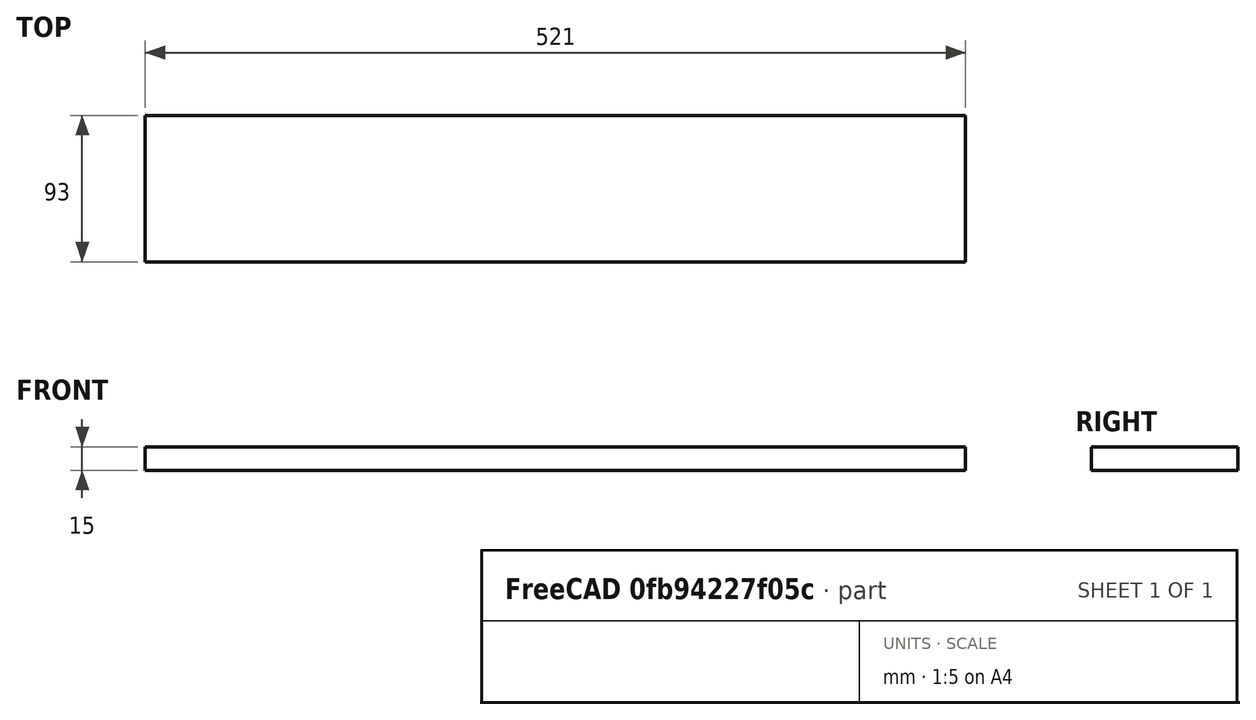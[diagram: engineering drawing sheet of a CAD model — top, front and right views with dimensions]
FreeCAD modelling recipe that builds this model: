
FCSTD DOCUMENT  (FreeCAD 1.0R39109 (Git))
Label: 17_drawer_96mm_front
License: All rights reserved
LicenseURL: http://en.wikipedia.org/wiki/All_rights_reserved
objects: Spreadsheet::Sheet×1, Sketcher::SketchObject×1, PartDesign::Pad×1, PartDesign::Body×1
note: 6 computed .brp shape members not serialized (recipe doc carries the construction recipe); baked Part::Feature solids carry a one-line shape summary decoded from their .brp

FEATURE [Spreadsheet::Sheet] Spreadsheet
  cells = A2='length; B2(length)=521; A3='width; B3(width)=93; A4='height; B4(height)=15; D9=433; D10==D9 + 30; E10==B2 - D10; E11==E10 / 2
FEATURE [Sketcher::SketchObject] Sketch
  ArcFitTolerance = 0
  AttachmentSupport = -> [XY_Plane]
  FullyConstrained = true
  MakeInternals = false
  MapMode = 5
  expr: Constraints[11] = Spreadsheet.length
  expr: Constraints[12] = Spreadsheet.width
  sketch-geometry (5):
    g0: LineSegment StartX=-260.5 StartY=46.5 StartZ=0 EndX=260.5 EndY=46.5 EndZ=0
    g1: LineSegment StartX=260.5 StartY=46.5 StartZ=0 EndX=260.5 EndY=-46.5 EndZ=0
    g2: LineSegment StartX=260.5 StartY=-46.5 StartZ=0 EndX=-260.5 EndY=-46.5 EndZ=0
    g3: LineSegment StartX=-260.5 StartY=-46.5 StartZ=0 EndX=-260.5 EndY=46.5 EndZ=0
    g4: LineSegment [constr] StartX=-260.5 StartY=46.5 StartZ=0 EndX=260.5 EndY=-46.5 EndZ=0
  constraints (13):
    c: Coincident(g0,g1)
    c: Coincident(g1,g2)
    c: Coincident(g2,g3)
    c: Coincident(g3,g0)
    c: Horizontal(g0)
    c: Horizontal(g2)
    c: Vertical(g1)
    c: Vertical(g3)
    c: Coincident(g4,g1)
    c: Coincident(g0,g4)
    c: Symmetric(g0,g1,g-1)
    c: Distance(g0,g0) = 521
    c: Distance(g0,g2) = 93
FEATURE [PartDesign::Pad] Pad
  Direction = (0,0,1)
  Length = 15
  Length2 = 10
  Profile = -> Sketch
  ReferenceAxis = -> Sketch [N_Axis]
  Suppressed = false
  Type = 0
  expr: Length = Spreadsheet.height
FEATURE [PartDesign::Body] Body
  AllowCompound = false
  Group = -> [Sketch,Pad]
  Origin = -> Origin
  Tip = -> Pad
